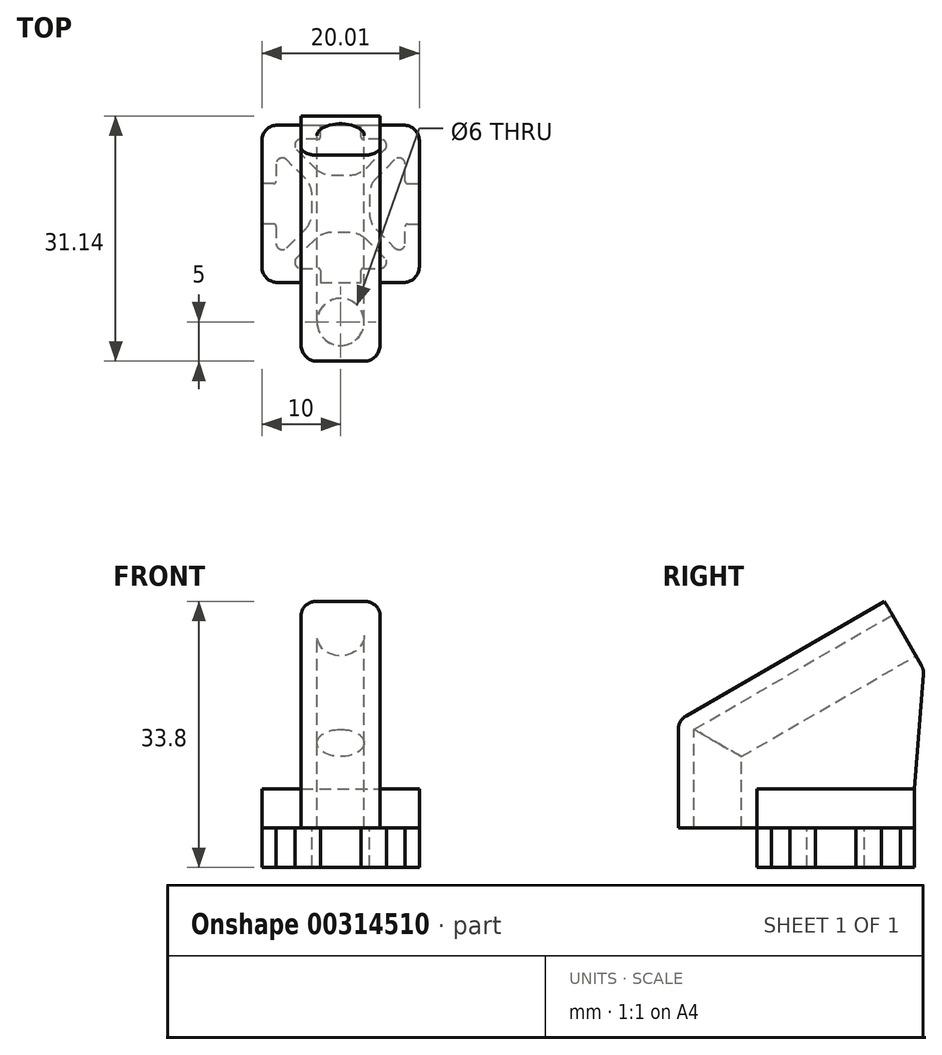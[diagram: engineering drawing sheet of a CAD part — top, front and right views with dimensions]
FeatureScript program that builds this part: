
annotation { "Feature Type Name" : "Feature", "Feature Type Description" : "" }
export const myFeature = defineFeature(function(context is Context, id is Id, definition is map)
    precondition{}
    {
        {
            var Q0;
            Q0=qCreatedBy(makeId("Top.planeOp"),FACE);
            var sketch = newSketch(context, id + "F0", { "sketchPlane" : qUnion([Q0])});
            skArc(sketch, "E0.0.0", {"start": v(1.15, -6.74) * mm, "mid": v(0.5, -7.72) * mm, "end": v(0.28, -8.87) * mm});
            skLineSegment(sketch, "E0.0.1", {"start": v(0.28, -8.87) * mm, "end": v(0.28, -11.13) * mm});
            skArc(sketch, "E0.0.2", {"start": v(0.28, -11.13) * mm, "mid": v(0.5, -12.28) * mm, "end": v(1.15, -13.26) * mm});
            skLineSegment(sketch, "E0.0.3", {"start": v(1.15, -13.26) * mm, "end": v(3.5, -15.6) * mm});
            skArc(sketch, "E0.0.4", {"start": v(3.5, -15.6) * mm, "mid": v(4.34, -15.76) * mm, "end": v(4.82, -15.04) * mm});
            skLineSegment(sketch, "E0.0.5", {"start": v(4.82, -15.04) * mm, "end": v(4.83, -12.87) * mm});
            skArc(sketch, "E0.0.6", {"start": v(4.83, -12.87) * mm, "mid": v(4.91, -12.66) * mm, "end": v(5.13, -12.57) * mm});
            skLineSegment(sketch, "E0.0.7", {"start": v(5.13, -12.57) * mm, "end": v(5.83, -12.57) * mm});
            skArc(sketch, "E0.0.8", {"start": v(5.83, -12.57) * mm, "mid": v(6.4, -12.8) * mm, "end": v(6.63, -13.37) * mm});
            skLineSegment(sketch, "E0.0.9", {"start": v(6.63, -13.37) * mm, "end": v(6.63, -18) * mm});
            skArc(sketch, "E0.0.10", {"start": v(6.63, -18) * mm, "mid": v(6.04, -19.41) * mm, "end": v(4.63, -20) * mm});
            skLineSegment(sketch, "E0.0.11", {"start": v(4.63, -20) * mm, "end": v(0, -20) * mm});
            skArc(sketch, "E0.0.12", {"start": v(0, -20) * mm, "mid": v(-0.57, -19.77) * mm, "end": v(-0.8, -19.2) * mm});
            skLineSegment(sketch, "E0.0.13", {"start": v(-0.8, -19.2) * mm, "end": v(-0.8, -18.5) * mm});
            skArc(sketch, "E0.0.14", {"start": v(-0.8, -18.5) * mm, "mid": v(-0.71, -18.29) * mm, "end": v(-0.5, -18.2) * mm});
            skLineSegment(sketch, "E0.0.15", {"start": v(-0.5, -18.2) * mm, "end": v(1.67, -18.2) * mm});
            skArc(sketch, "E0.0.16", {"start": v(1.67, -18.2) * mm, "mid": v(2.39, -17.72) * mm, "end": v(2.22, -16.87) * mm});
            skLineSegment(sketch, "E0.0.17", {"start": v(2.22, -16.87) * mm, "end": v(-0.12, -14.53) * mm});
            skArc(sketch, "E0.0.18", {"start": v(-0.12, -14.53) * mm, "mid": v(-1.1, -13.88) * mm, "end": v(-2.24, -13.65) * mm});
            skLineSegment(sketch, "E0.0.19", {"start": v(-2.24, -13.65) * mm, "end": v(-4.5, -13.65) * mm});
            skArc(sketch, "E0.0.20", {"start": v(-4.5, -13.65) * mm, "mid": v(-5.66, -13.88) * mm, "end": v(-6.63, -14.53) * mm});
            skLineSegment(sketch, "E0.0.21", {"start": v(-6.63, -14.53) * mm, "end": v(-8.97, -16.87) * mm});
            skArc(sketch, "E0.0.22", {"start": v(-8.97, -16.87) * mm, "mid": v(-9.14, -17.72) * mm, "end": v(-8.42, -18.2) * mm});
            skLineSegment(sketch, "E0.0.23", {"start": v(-8.42, -18.2) * mm, "end": v(-6.25, -18.2) * mm});
            skArc(sketch, "E0.0.24", {"start": v(-6.25, -18.2) * mm, "mid": v(-6.04, -18.29) * mm, "end": v(-5.95, -18.5) * mm});
            skLineSegment(sketch, "E0.0.25", {"start": v(-5.95, -18.5) * mm, "end": v(-5.95, -19.2) * mm});
            skArc(sketch, "E0.0.26", {"start": v(-5.95, -19.2) * mm, "mid": v(-6.18, -19.77) * mm, "end": v(-6.75, -20) * mm});
            skLineSegment(sketch, "E0.0.27", {"start": v(-6.75, -20) * mm, "end": v(-11.38, -20) * mm});
            skArc(sketch, "E0.0.28", {"start": v(-11.38, -20) * mm, "mid": v(-12.79, -19.41) * mm, "end": v(-13.38, -18) * mm});
            skLineSegment(sketch, "E0.0.29", {"start": v(-13.38, -18) * mm, "end": v(-13.38, -13.38) * mm});
            skArc(sketch, "E0.0.30", {"start": v(-13.38, -13.38) * mm, "mid": v(-13.14, -12.8) * mm, "end": v(-12.57, -12.57) * mm});
            skLineSegment(sketch, "E0.0.31", {"start": v(-12.57, -12.57) * mm, "end": v(-11.88, -12.57) * mm});
            skArc(sketch, "E0.0.32", {"start": v(-11.88, -12.57) * mm, "mid": v(-11.66, -12.66) * mm, "end": v(-11.58, -12.87) * mm});
            skLineSegment(sketch, "E0.0.33", {"start": v(-11.58, -12.87) * mm, "end": v(-11.57, -15.04) * mm});
            skArc(sketch, "E0.0.34", {"start": v(-11.57, -15.04) * mm, "mid": v(-11.1, -15.76) * mm, "end": v(-10.24, -15.6) * mm});
            skLineSegment(sketch, "E0.0.35", {"start": v(-10.24, -15.6) * mm, "end": v(-7.9, -13.26) * mm});
            skArc(sketch, "E0.0.36", {"start": v(-7.9, -13.26) * mm, "mid": v(-7.25, -12.28) * mm, "end": v(-7.03, -11.13) * mm});
            skLineSegment(sketch, "E0.0.37", {"start": v(-7.03, -11.13) * mm, "end": v(-7.03, -8.87) * mm});
            skArc(sketch, "E0.0.38", {"start": v(-7.03, -8.87) * mm, "mid": v(-7.25, -7.72) * mm, "end": v(-7.9, -6.74) * mm});
            skLineSegment(sketch, "E0.0.39", {"start": v(-7.9, -6.74) * mm, "end": v(-10.24, -4.4) * mm});
            skArc(sketch, "E0.0.40", {"start": v(-10.24, -4.4) * mm, "mid": v(-11.1, -4.24) * mm, "end": v(-11.57, -4.96) * mm});
            skLineSegment(sketch, "E0.0.41", {"start": v(-11.57, -4.96) * mm, "end": v(-11.58, -7.13) * mm});
            skArc(sketch, "E0.0.42", {"start": v(-11.58, -7.13) * mm, "mid": v(-11.66, -7.34) * mm, "end": v(-11.88, -7.43) * mm});
            skLineSegment(sketch, "E0.0.43", {"start": v(-11.88, -7.43) * mm, "end": v(-12.58, -7.43) * mm});
            skArc(sketch, "E0.0.44", {"start": v(-12.58, -7.43) * mm, "mid": v(-13.14, -7.2) * mm, "end": v(-13.38, -6.63) * mm});
            skLineSegment(sketch, "E0.0.45", {"start": v(-13.38, -6.63) * mm, "end": v(-13.38, -2) * mm});
            skArc(sketch, "E0.0.46", {"start": v(-13.38, -2) * mm, "mid": v(-12.79, -0.59) * mm, "end": v(-11.38, 0) * mm});
            skLineSegment(sketch, "E0.0.47", {"start": v(-11.38, 0) * mm, "end": v(-6.75, 0) * mm});
            skArc(sketch, "E0.0.48", {"start": v(-6.75, 0) * mm, "mid": v(-6.18, -0.23) * mm, "end": v(-5.95, -0.8) * mm});
            skLineSegment(sketch, "E0.0.49", {"start": v(-5.95, -0.8) * mm, "end": v(-5.95, -1.5) * mm});
            skArc(sketch, "E0.0.50", {"start": v(-5.95, -1.5) * mm, "mid": v(-6.04, -1.71) * mm, "end": v(-6.25, -1.8) * mm});
            skLineSegment(sketch, "E0.0.51", {"start": v(-6.25, -1.8) * mm, "end": v(-8.42, -1.8) * mm});
            skArc(sketch, "E0.0.52", {"start": v(-8.42, -1.8) * mm, "mid": v(-9.14, -2.28) * mm, "end": v(-8.97, -3.13) * mm});
            skLineSegment(sketch, "E0.0.53", {"start": v(-8.97, -3.13) * mm, "end": v(-6.63, -5.47) * mm});
            skArc(sketch, "E0.0.54", {"start": v(-6.63, -5.47) * mm, "mid": v(-5.66, -6.12) * mm, "end": v(-4.5, -6.35) * mm});
            skLineSegment(sketch, "E0.0.55", {"start": v(-4.5, -6.35) * mm, "end": v(-2.24, -6.35) * mm});
            skArc(sketch, "E0.0.56", {"start": v(-2.24, -6.35) * mm, "mid": v(-1.1, -6.12) * mm, "end": v(-0.12, -5.47) * mm});
            skLineSegment(sketch, "E0.0.57", {"start": v(-0.12, -5.47) * mm, "end": v(2.22, -3.13) * mm});
            skArc(sketch, "E0.0.58", {"start": v(2.22, -3.13) * mm, "mid": v(2.39, -2.28) * mm, "end": v(1.67, -1.8) * mm});
            skLineSegment(sketch, "E0.0.59", {"start": v(1.67, -1.8) * mm, "end": v(-0.5, -1.8) * mm});
            skArc(sketch, "E0.0.60", {"start": v(-0.5, -1.8) * mm, "mid": v(-0.71, -1.71) * mm, "end": v(-0.8, -1.5) * mm});
            skLineSegment(sketch, "E0.0.61", {"start": v(-0.8, -1.5) * mm, "end": v(-0.8, -0.8) * mm});
            skArc(sketch, "E0.0.62", {"start": v(-0.8, -0.8) * mm, "mid": v(-0.57, -0.23) * mm, "end": v(0, 0) * mm});
            skLineSegment(sketch, "E0.0.63", {"start": v(0, 0) * mm, "end": v(4.62, 0) * mm});
            skArc(sketch, "E0.0.64", {"start": v(4.62, 0) * mm, "mid": v(6.04, -0.59) * mm, "end": v(6.62, -2) * mm});
            skLineSegment(sketch, "E0.0.65", {"start": v(6.62, -2) * mm, "end": v(6.62, -6.63) * mm});
            skArc(sketch, "E0.0.66", {"start": v(6.62, -6.63) * mm, "mid": v(6.4, -7.2) * mm, "end": v(5.83, -7.42) * mm});
            skLineSegment(sketch, "E0.0.67", {"start": v(5.83, -7.42) * mm, "end": v(5.13, -7.42) * mm});
            skArc(sketch, "E0.0.68", {"start": v(5.13, -7.42) * mm, "mid": v(4.91, -7.34) * mm, "end": v(4.83, -7.13) * mm});
            skLineSegment(sketch, "E0.0.69", {"start": v(4.83, -7.13) * mm, "end": v(4.82, -4.96) * mm});
            skArc(sketch, "E0.0.70", {"start": v(4.82, -4.96) * mm, "mid": v(4.34, -4.24) * mm, "end": v(3.5, -4.4) * mm});
            skLineSegment(sketch, "E0.0.71", {"start": v(3.5, -4.4) * mm, "end": v(1.15, -6.74) * mm});
            skLineSegment(sketch, "E1", {"start": v(-5.95, -19.2) * mm, "end": v(-5.95, -20) * mm});
            skLineSegment(sketch, "E2", {"start": v(-5.95, -20) * mm, "end": v(-0.8, -20) * mm});
            skLineSegment(sketch, "E3", {"start": v(-0.8, -20) * mm, "end": v(-0.8, -19.2) * mm});
            skLineSegment(sketch, "E4", {"start": v(-12.57, -12.57) * mm, "end": v(-13.38, -12.57) * mm});
            skLineSegment(sketch, "E5", {"start": v(-13.38, -12.57) * mm, "end": v(-13.38, -7.43) * mm});
            skLineSegment(sketch, "E6", {"start": v(-13.38, -7.43) * mm, "end": v(-12.58, -7.43) * mm});
            skLineSegment(sketch, "E7", {"start": v(-5.95, -0.8) * mm, "end": v(-5.95, 0) * mm});
            skLineSegment(sketch, "E8", {"start": v(-5.95, 0) * mm, "end": v(-0.8, 0) * mm});
            skLineSegment(sketch, "E9", {"start": v(-0.8, 0) * mm, "end": v(-0.8, -0.8) * mm});
            skLineSegment(sketch, "E10", {"start": v(5.83, -7.42) * mm, "end": v(6.62, -7.42) * mm});
            skLineSegment(sketch, "E11", {"start": v(6.62, -7.42) * mm, "end": v(6.62, -12.57) * mm});
            skLineSegment(sketch, "E12", {"start": v(6.62, -12.57) * mm, "end": v(5.83, -12.57) * mm});
            skSolve(sketch);
        }
        {
            var Q0;
            Q0=makeQuery(id+"F0.imprint","IMPRINT",FACE,{"disambiguationData":[TD([[makeQuery(id+"F0.imprint","IMPRINT",EDGE,{"derivedFrom":sQuery(id+"F0.wireOp",EDGE,"E0.0.31")}),1.0]])]});
            var Q1;
            Q1=makeQuery(id+"F0.imprint","IMPRINT",FACE,{"disambiguationData":[TD([[makeQuery(id+"F0.imprint","IMPRINT",EDGE,{"derivedFrom":sQuery(id+"F0.wireOp",EDGE,"E0.0.13")}),1.0]])]});
            var Q2;
            Q2=makeQuery(id+"F0.imprint","IMPRINT",FACE,{"disambiguationData":[TD([[makeQuery(id+"F0.imprint","IMPRINT",EDGE,{"derivedFrom":sQuery(id+"F0.wireOp",EDGE,"E0.0.0")}),1.0]])]});
            var Q3;
            Q3=makeQuery(id+"F0.imprint","IMPRINT",FACE,{"disambiguationData":[TD([[makeQuery(id+"F0.imprint","IMPRINT",EDGE,{"derivedFrom":sQuery(id+"F0.wireOp",EDGE,"E0.0.49")}),1.0]])]});
            extrude(context, id + "F1", {"entities" : qUnion([Q0, Q1, Q2, Q3]), "oppositeDirection" : true, "depth" : 5 * mm});
        }
        {
            var Q0;
            Q0=makeQuery(id+"F1.opExtrude","CAP_FACE",FACE,{"disambiguationData":[OSD([sQuery(id+"F0.wireOp",EDGE,"E0.0.0"),sQuery(id+"F0.wireOp",EDGE,"E0.0.1"),sQuery(id+"F0.wireOp",EDGE,"E0.0.2"),sQuery(id+"F0.wireOp",EDGE,"E0.0.3"),sQuery(id+"F0.wireOp",EDGE,"E0.0.4"),sQuery(id+"F0.wireOp",EDGE,"E0.0.5"),sQuery(id+"F0.wireOp",EDGE,"E0.0.6"),sQuery(id+"F0.wireOp",EDGE,"E0.0.7"),sQuery(id+"F0.wireOp",EDGE,"E0.0.67"),sQuery(id+"F0.wireOp",EDGE,"E0.0.68"),sQuery(id+"F0.wireOp",EDGE,"E0.0.69"),sQuery(id+"F0.wireOp",EDGE,"E0.0.70"),sQuery(id+"F0.wireOp",EDGE,"E0.0.71"),sQuery(id+"F0.wireOp",EDGE,"E10"),sQuery(id+"F0.wireOp",EDGE,"E11"),sQuery(id+"F0.wireOp",EDGE,"E12")])],"isStart":true});
            var sketch = newSketch(context, id + "F2", { "sketchPlane" : qUnion([Q0])});
            skLineSegment(sketch, "E13", {"start": v(6.62, -10) * mm, "end": v(-13.4, -10) * mm, "construction": true});
            skLineSegment(sketch, "E14.bottom", {"start": v(-13.39, -20) * mm, "end": v(6.61, -20) * mm});
            skLineSegment(sketch, "E14.top", {"start": v(-13.39, 0) * mm, "end": v(6.61, 0) * mm});
            skLineSegment(sketch, "E14.left", {"start": v(-13.39, -20) * mm, "end": v(-13.39, 0) * mm});
            skLineSegment(sketch, "E14.right", {"start": v(6.61, -20) * mm, "end": v(6.61, 0) * mm});
            skPoint(sketch, "E14.middle", {"position": v(-3.39, -10) * mm});
            skSolve(sketch);
        }
        {
            var Q0;
            Q0 = qSketchRegion(id + "F2", true);
            extrude(context, id + "F3", {"entities" : qUnion([Q0]), "depth" : 5 * mm});
        }
        {
            var Q0;
            Q0=makeQuery(id+"F3.opExtrude","SWEPT_FACE",FACE,{"disambiguationData":[OSD([sQuery(id+"F2.wireOp",EDGE,"E14.right")])]});
            cPlane(context, id + "F4", {"entities" : qUnion([Q0]), "cplaneType" : CPlaneType.OFFSET, "offset" : 10 * mm, "oppositeDirection" : true, "width" : 150 * mm, "height" : 150 * mm});
        }
        {
            var Q0;
            Q0=qCreatedBy(id+"F4.planeOp",FACE);
            var sketch = newSketch(context, id + "F5", { "sketchPlane" : qUnion([Q0])});
            skLineSegment(sketch, "E15", {"start": v(-25, 0) * mm, "end": v(-25, 10.8) * mm});
            skLineSegment(sketch, "E16", {"start": v(-25, 10.8) * mm, "end": v(-1.32, 24.47) * mm});
            skSolve(sketch);
        }
        {
            var Q0;
            Q0=qCreatedBy(makeId("Top.planeOp"),FACE);
            var sketch = newSketch(context, id + "F6", { "sketchPlane" : qUnion([Q0])});
            skLineSegment(sketch, "E17.bottom", {"start": v(-8.39, -30) * mm, "end": v(1.61, -30) * mm});
            skLineSegment(sketch, "E17.top", {"start": v(-8.39, -20) * mm, "end": v(1.61, -20) * mm});
            skLineSegment(sketch, "E17.left", {"start": v(-8.39, -30) * mm, "end": v(-8.39, -20) * mm});
            skLineSegment(sketch, "E17.right", {"start": v(1.61, -30) * mm, "end": v(1.61, -20) * mm});
            skPoint(sketch, "E17.middle", {"position": v(-3.39, -25) * mm});
            skCircle(sketch, "E18", {"center": v(-3.39, -25) * mm, "radius": 3 * mm});
            skSolve(sketch);
        }
        {
            var Q0;
            Q0=makeQuery(id+"F6.imprint","IMPRINT",FACE,{"disambiguationData":[TD([[makeQuery(id+"F6.imprint","IMPRINT",EDGE,{"derivedFrom":sQuery(id+"F6.wireOp",EDGE,"E17.bottom")}),1.0]])]});
            var Q1;
            Q1 = qConstructionFilter(qBodyType(qCreatedBy(id + "F5" ,EDGE), BodyType.WIRE), ConstructionObject.NO);
            sweep(context, id + "F7", {"operationType" : NewBodyOperationType.ADD, "profiles" : qUnion([Q0]), "path" : qUnion([Q1])});
        }
        {
            var Q0;
            Q0=makeQuery(id+"F7.opSweep","SWEPT_FACE",FACE,{"disambiguationData":[OSD([sQuery(id+"F5.wireOp",EDGE,"E15"),sQuery(id+"F6.wireOp",EDGE,"E17.right")])]});
            var sketch = newSketch(context, id + "F8", { "sketchPlane" : qUnion([Q0])});
            skLineSegment(sketch, "E19", {"start": v(1.18, 20.14) * mm, "end": v(-20, 7.91) * mm});
            skLineSegment(sketch, "E20", {"start": v(-20, 7.91) * mm, "end": v(-20, 5) * mm});
            skLineSegment(sketch, "E21", {"start": v(-20, 5) * mm, "end": v(0, 5) * mm});
            skLineSegment(sketch, "E22", {"start": v(0, 5) * mm, "end": v(1.18, 20.14) * mm});
            skSolve(sketch);
        }
        {
            var Q0;
            Q0=makeQuery(id+"F8.imprint","IMPRINT",FACE,{"disambiguationData":[TD([[makeQuery(id+"F8.imprint","IMPRINT",EDGE,{"derivedFrom":sQuery(id+"F8.wireOp",EDGE,"E19")}),-1.0]])]});
            extrude(context, id + "F9", {"entities" : qUnion([Q0]), "operationType" : NewBodyOperationType.ADD, "oppositeDirection" : true, "depth" : 10 * mm});
        }
        {
            var Q0;
            Q0=makeQuery(id+"F3.opExtrude","SWEPT_EDGE",EDGE,{"disambiguationData":[OSD([sQuery(id+"F2.wireOp",EDGE,"E14.top"),sQuery(id+"F2.wireOp",EDGE,"E14.right")])]});
            var Q1;
            Q1=makeQuery(id+"F3.opExtrude","SWEPT_EDGE",EDGE,{"disambiguationData":[OSD([sQuery(id+"F2.wireOp",EDGE,"E14.bottom"),sQuery(id+"F2.wireOp",EDGE,"E14.right")])]});
            var Q2;
            Q2=makeQuery(id+"F3.opExtrude","SWEPT_EDGE",EDGE,{"disambiguationData":[OSD([sQuery(id+"F2.wireOp",EDGE,"E14.top"),sQuery(id+"F2.wireOp",EDGE,"E14.left")])]});
            var Q3;
            Q3=makeQuery(id+"F3.opExtrude","SWEPT_EDGE",EDGE,{"disambiguationData":[OSD([sQuery(id+"F2.wireOp",EDGE,"E14.bottom"),sQuery(id+"F2.wireOp",EDGE,"E14.left")])]});
            var Q4;
            Q4=makeQuery(id+"F7.opSweep","SWEPT_EDGE",EDGE,{"disambiguationData":[OSD([sQuery(id+"F5.wireOp",EDGE,"E15"),sQuery(id+"F6.wireOp",EDGE,"E17.bottom"),sQuery(id+"F6.wireOp",EDGE,"E17.left")])]});
            var Q5;
            Q5=makeQuery(id+"F7.opSweep","SWEPT_EDGE",EDGE,{"disambiguationData":[OSD([sQuery(id+"F5.wireOp",EDGE,"E15"),sQuery(id+"F6.wireOp",EDGE,"E17.bottom"),sQuery(id+"F6.wireOp",EDGE,"E17.right")])]});
            var Q6;
            Q6=makeQuery(id+"F7.opSweep","SWEPT_EDGE",EDGE,{"disambiguationData":[OSD([sQuery(id+"F5.wireOp",EDGE,"E16"),sQuery(id+"F6.wireOp",EDGE,"E17.bottom"),sQuery(id+"F6.wireOp",EDGE,"E17.left")])]});
            var Q7;
            Q7=makeQuery(id+"F7.opSweep","SWEPT_EDGE",EDGE,{"disambiguationData":[OSD([sQuery(id+"F5.wireOp",EDGE,"E16"),sQuery(id+"F6.wireOp",EDGE,"E17.bottom"),sQuery(id+"F6.wireOp",EDGE,"E17.right")])]});
            var Q8;
            Q8=makeQuery(id+"F7.opSweep","MID_CAP_EDGE",EDGE,{"disambiguationData":[OSD([sQuery(id+"F5.wireOp",VERTEX,"E16.start"),sQuery(id+"F6.wireOp",EDGE,"E17.bottom")])],"capPos":1.0});
            var Q9;
            {var subQ0=sQuery(id+"F6.wireOp",EDGE,"E17.left");var subQ1=sQuery(id+"F5.wireOp",EDGE,"E15");Q9=makeQuery(id+"F7.boolean.opBoolean","SPLIT",EDGE,{"disambiguationData":[topologyDisambiguationEdgeConnected([makeQuery(id+"F3.opExtrude","SWEPT_FACE",FACE,{"disambiguationData":[OSD([sQuery(id+"F2.wireOp",EDGE,"E14.bottom")])]})])],"derivedFrom":makeQuery(id+"F7.opSweep","SWEPT_EDGE",EDGE,{"disambiguationData":[OSD([subQ1,sQuery(id+"F6.wireOp",EDGE,"E17.top"),subQ0])]})});}
            var Q10;
            {var subQ0=sQuery(id+"F6.wireOp",EDGE,"E17.right");var subQ1=sQuery(id+"F5.wireOp",EDGE,"E15");Q10=makeQuery(id+"F7.boolean.opBoolean","SPLIT",EDGE,{"disambiguationData":[topologyDisambiguationEdgeConnected([makeQuery(id+"F3.opExtrude","SWEPT_FACE",FACE,{"disambiguationData":[OSD([sQuery(id+"F2.wireOp",EDGE,"E14.bottom")])]})])],"derivedFrom":makeQuery(id+"F7.opSweep","SWEPT_EDGE",EDGE,{"disambiguationData":[OSD([subQ1,sQuery(id+"F6.wireOp",EDGE,"E17.top"),subQ0])]})});}
            var Q11;
            Q11=makeQuery(id+"F9.opExtrude","CAP_EDGE",EDGE,{"disambiguationData":[OSD([sQuery(id+"F8.wireOp",EDGE,"E21")])],"isStart":true});
            var Q12;
            Q12=makeQuery(id+"F9.opExtrude","CAP_EDGE",EDGE,{"disambiguationData":[OSD([sQuery(id+"F8.wireOp",EDGE,"E21")])],"isStart":false});
            var Q13;
            {var subQ0=sQuery(id+"F5.wireOp",VERTEX,"E16.end");Q13=makeQuery(id+"F9.boolean.opBoolean","MERGE",EDGE,{"derivedFrom":[makeQuery(id+"F7.opSweep","CAP_EDGE",EDGE,{"disambiguationData":[OSD([subQ0,sQuery(id+"F6.wireOp",EDGE,"E17.top")])],"isStart":false}),makeQuery(id+"F9.opExtrude","SWEPT_EDGE",EDGE,{"disambiguationData":[OSD([subQ0,sQuery(id+"F6.wireOp",EDGE,"E17.right"),sQuery(id+"F8.wireOp",EDGE,"E19"),sQuery(id+"F8.wireOp",EDGE,"E22")])]})]});}
            fillet(context, id + "F10", {"entities" : qUnion([Q0, Q1, Q2, Q3, Q4, Q5, Q6, Q7, Q8, Q9, Q10, Q11, Q12, Q13]), "radius" : 2 * mm, "tangentPropagation" : true, "allowEdgeOverflow" : false});
        }
    });
